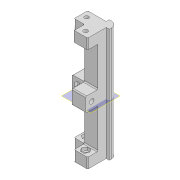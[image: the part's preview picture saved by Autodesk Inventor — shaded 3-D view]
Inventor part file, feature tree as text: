
AUTODESK INVENTOR PART (.ipt)
format: ipt  version: 2020 (Build 240168000, 168)  size: 324,608 bytes
history: native  units: mm
features: extrude x12, sketch x12, other x6, fillet x2
ambient origin geometry x8: Origin, YZ Plane, XZ Plane, XY Plane, X Axis, Y Axis, Z Axis, Center Point
bodies: Body1 (feature_tree)
feature tree (32):
  other  "Sólido1"
  extrude  "Extrusão1"  Depth=16.0mm
  extrude  "Extrusão2"  Depth=3.0mm
  extrude  "Extrusão3"  Depth=3.0mm
  extrude  "Extrusão4"  Depth=5.2mm
  extrude  "Extrusão5"  Depth=8.0mm
  fillet  "Arredondamento1"  Radius=110.0mm
  extrude  "Extrusão6"  Depth=10.0mm
  extrude  "Extrusão7"  TaperAngle=0.0deg  [1 undecoded]
  other  "Plano de trabalho1"
  extrude  "Extrusão9"  Depth=5.0mm
  extrude  "Extrusão10"  Depth=10.0mm
  extrude  "Extrusão11"  Depth=10.0mm
  extrude  "Extrusão12"  Depth=5.0mm
  extrude  "Extrusão13"  Depth=1.0mm TaperAngle=0.0deg
  fillet  "Arredondamento2"  Radius=1.0mm
  sketch  "Esboço1"  dims[d0=16.0mm d1=16.0mm]
  sketch  "Esboço2"  dims[d2=8.0mm d3=3.0mm]
  sketch  "Esboço3"  dims[d4=8.0mm d5=3.0mm]
  sketch  "Esboço4"  dims[d6=6.0mm d7=5.2mm]
  sketch  "Esboço5"  dims[d8=8.0mm d9=8.0mm d10=110.0mm d11=0.0mm]
  sketch  "Esboço6"  dims[d12=10.0mm d13=10.0mm]
  sketch  "Esboço7"  dims[d14=10.0mm d15=0.0mm d16=0.0mm]
  other  "Contorno projetado1"
  other  "Contorno projetado2"
  sketch  "Esboço9"  dims[d17=4.0mm d18=5.0mm]
  other  "Contorno projetado3"
  other  "Contorno projetado4"
  sketch  "Esboço10"  dims[d19=200.0mm d20=0.0mm d21=10.0mm]
  sketch  "Esboço11"  dims[d22=10.0mm d23=0.0mm d24=4.0mm]
  sketch  "Esboço12"  dims[d25=5.0mm d26=7.0mm]
  sketch  "Esboço13"  dims[d27=6.0mm d28=200.0mm d29=0.0mm d30=1.0mm d31=13.0mm d32=6.8mm d33=6.8mm d34=3.0mm d35=0.0mm d36=3.0mm d37=0.0mm d38=0.0mm d44=0.0mm d45=-50.0mm d46=12.0mm d47=12.0mm d48=2.0mm d49=0.0mm d50=12.0mm d51=0.0mm d52=4.5mm d53=6.0mm d54=20.0mm d55=0.0mm d56=4.5mm d57=6.0mm d58=20.0mm d59=0.0mm d60=6.8mm d61=3.0mm d62=0.0mm d63=6.8mm d64=3.0mm d65=0.0mm d66=1.0mm]
note: 1 required parameter value undecoded (feature->parameter linkage not recoverable at this tier; creation-order binding heuristic only, values carry confidence <= 0.55)
